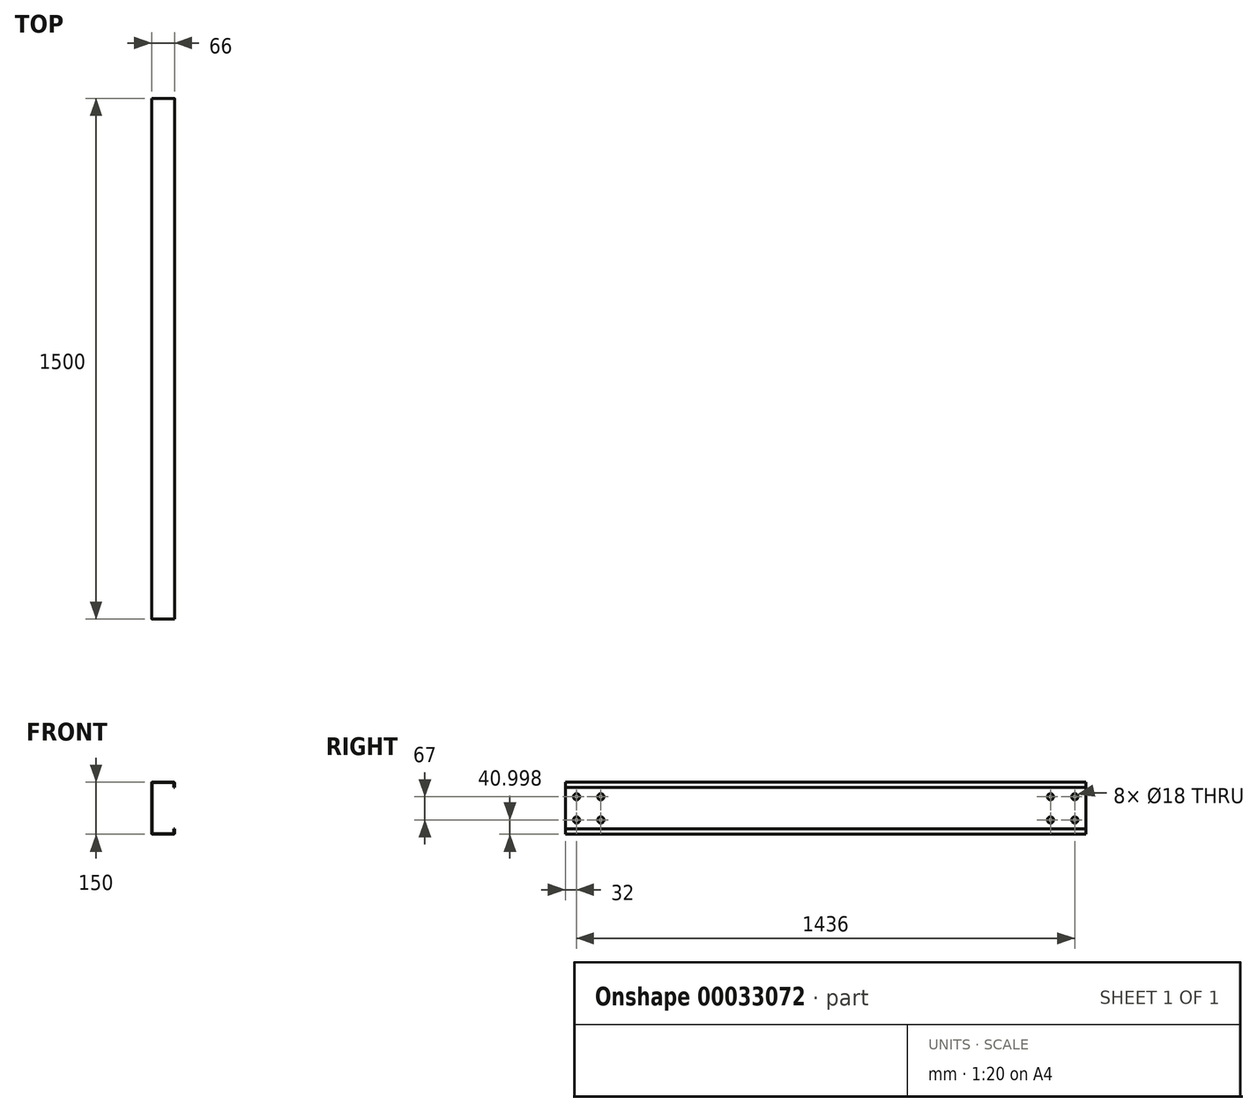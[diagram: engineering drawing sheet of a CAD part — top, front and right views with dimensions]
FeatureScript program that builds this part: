
annotation { "Feature Type Name" : "Feature", "Feature Type Description" : "" }
export const myFeature = defineFeature(function(context is Context, id is Id, definition is map)
    precondition{}
    {
        {
            var Q0;
            Q0=qCreatedBy(makeId("Front.planeOp"),FACE);
            var sketch = newSketch(context, id + "F0", { "sketchPlane" : qUnion([Q0])});
            skLineSegment(sketch, "E0", {"start": v(6.96, 61.06) * mm, "end": v(6.96, 76.06) * mm});
            skLineSegment(sketch, "E1", {"start": v(6.96, 76.06) * mm, "end": v(-59.04, 76.06) * mm});
            skLineSegment(sketch, "E2", {"start": v(-59.04, 76.06) * mm, "end": v(-59.04, -73.94) * mm});
            skLineSegment(sketch, "E3", {"start": v(-59.04, -73.94) * mm, "end": v(6.96, -73.94) * mm});
            skLineSegment(sketch, "E4", {"start": v(6.96, -73.94) * mm, "end": v(6.96, -58.94) * mm});
            skLineSegment(sketch, "E5", {"start": v(6.96, -58.94) * mm, "end": v(5.46, -58.94) * mm});
            skLineSegment(sketch, "E6", {"start": v(5.46, -58.94) * mm, "end": v(5.46, -72.44) * mm});
            skLineSegment(sketch, "E7", {"start": v(5.46, -72.44) * mm, "end": v(-57.54, -72.44) * mm});
            skLineSegment(sketch, "E8", {"start": v(-57.54, -72.44) * mm, "end": v(-57.54, 74.56) * mm});
            skLineSegment(sketch, "E9", {"start": v(-57.54, 74.56) * mm, "end": v(5.46, 74.56) * mm});
            skLineSegment(sketch, "E10", {"start": v(5.46, 74.56) * mm, "end": v(5.46, 61.22) * mm});
            skLineSegment(sketch, "E11", {"start": v(5.46, 61.22) * mm, "end": v(6.96, 61.06) * mm});
            skSolve(sketch);
        }
        {
            var Q0;
            Q0=makeQuery(id+"F0.imprint","IMPRINT",FACE,{"disambiguationData":[TD([[makeQuery(id+"F0.imprint","IMPRINT",EDGE,{"derivedFrom":sQuery(id+"F0.wireOp",EDGE,"E0")}),1.0]])]});
            extrude(context, id + "F1", {"entities" : qUnion([Q0]), "oppositeDirection" : true, "depth" : 1500 * mm});
        }
        {
            var Q0;
            Q0=makeQuery(id+"F1.opExtrude","SWEPT_EDGE",EDGE,{"disambiguationData":[OSD([sQuery(id+"F0.wireOp",EDGE,"E1"),sQuery(id+"F0.wireOp",EDGE,"E2")])]});
            var Q1;
            Q1=makeQuery(id+"F1.opExtrude","SWEPT_EDGE",EDGE,{"disambiguationData":[OSD([sQuery(id+"F0.wireOp",EDGE,"E0"),sQuery(id+"F0.wireOp",EDGE,"E1")])]});
            var Q2;
            Q2=makeQuery(id+"F1.opExtrude","SWEPT_EDGE",EDGE,{"disambiguationData":[OSD([sQuery(id+"F0.wireOp",EDGE,"E3"),sQuery(id+"F0.wireOp",EDGE,"E4")])]});
            var Q3;
            Q3=makeQuery(id+"F1.opExtrude","SWEPT_EDGE",EDGE,{"disambiguationData":[OSD([sQuery(id+"F0.wireOp",EDGE,"E2"),sQuery(id+"F0.wireOp",EDGE,"E3")])]});
            fillet(context, id + "F2", {"entities" : qUnion([Q0, Q1, Q2, Q3]), "radius" : 1.5 * mm, "tangentPropagation" : true, "allowEdgeOverflow" : false});
        }
        {
            var Q0;
            Q0=makeQuery(id+"F1.opExtrude","SWEPT_FACE",FACE,{"disambiguationData":[OSD([sQuery(id+"F0.wireOp",EDGE,"E8")])]});
            var sketch = newSketch(context, id + "F3", { "sketchPlane" : qUnion([Q0])});
            skPoint(sketch, "E12", {"position": v(32, 34.06) * mm});
            skPoint(sketch, "E13", {"position": v(102, 34.06) * mm});
            skPoint(sketch, "E14", {"position": v(102, -32.94) * mm});
            skPoint(sketch, "E15", {"position": v(32, -32.94) * mm});
            skPoint(sketch, "E16", {"position": v(1468, -32.94) * mm});
            skPoint(sketch, "E17", {"position": v(1398, -32.94) * mm});
            skPoint(sketch, "E18", {"position": v(1398, 34.06) * mm});
            skPoint(sketch, "E19", {"position": v(1468, 34.06) * mm});
            skSolve(sketch);
        }
        {
            var Q0;
            Q0=sQuery(id+"F3.wireOp",VERTEX,"E12");
            var Q1;
            Q1=sQuery(id+"F3.wireOp",VERTEX,"E13");
            var Q2;
            Q2=sQuery(id+"F3.wireOp",VERTEX,"E15");
            var Q3;
            Q3=sQuery(id+"F3.wireOp",VERTEX,"E14");
            var Q4;
            Q4=sQuery(id+"F3.wireOp",VERTEX,"E19");
            var Q5;
            Q5=sQuery(id+"F3.wireOp",VERTEX,"E18");
            var Q6;
            Q6=sQuery(id+"F3.wireOp",VERTEX,"E17");
            var Q7;
            Q7=sQuery(id+"F3.wireOp",VERTEX,"E16");
            var Q8;
            Q8=makeQuery(id+"F1.opExtrude","SWEPT_BODY",BODY,{"disambiguationData":[OSD([sQuery(id+"F0.wireOp",EDGE,"E0"),sQuery(id+"F0.wireOp",EDGE,"E1"),sQuery(id+"F0.wireOp",EDGE,"E2"),sQuery(id+"F0.wireOp",EDGE,"E3"),sQuery(id+"F0.wireOp",EDGE,"E4"),sQuery(id+"F0.wireOp",EDGE,"E5"),sQuery(id+"F0.wireOp",EDGE,"E6"),sQuery(id+"F0.wireOp",EDGE,"E7"),sQuery(id+"F0.wireOp",EDGE,"E8"),sQuery(id+"F0.wireOp",EDGE,"E9"),sQuery(id+"F0.wireOp",EDGE,"E10"),sQuery(id+"F0.wireOp",EDGE,"E11")])]});
            hole(context, id + "F4", {"style" : HoleStyle.SIMPLE, "holeDiameter" : 18 * mm, "endStyle" : HoleEndStyle.THROUGH, "locations" : qUnion([Q0, Q1, Q2, Q3, Q4, Q5, Q6, Q7]), "scope" : qUnion([Q8])});
        }
    });
